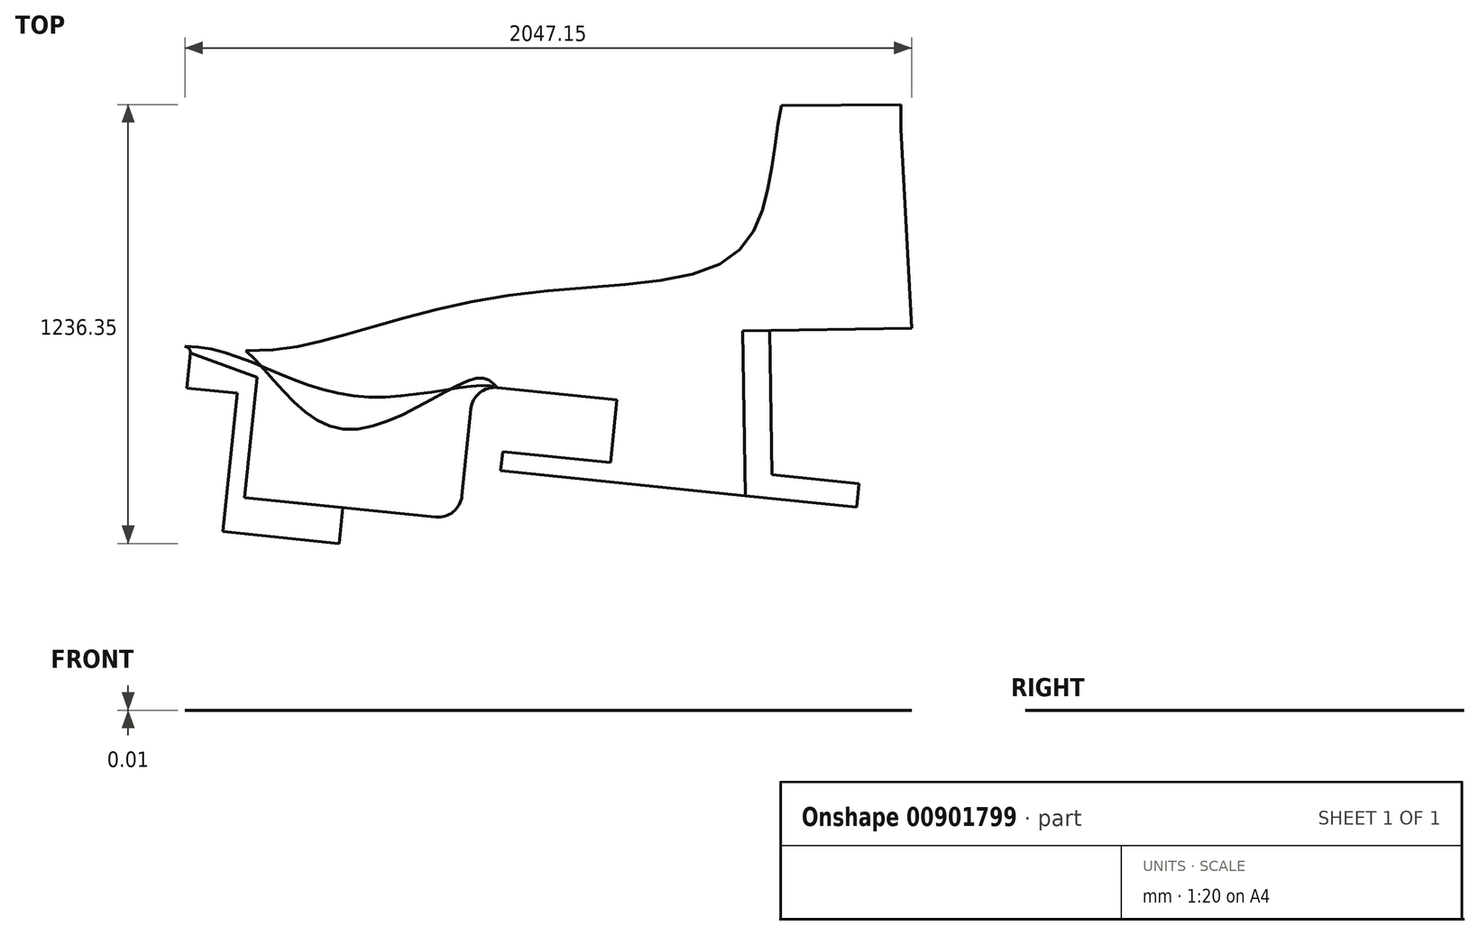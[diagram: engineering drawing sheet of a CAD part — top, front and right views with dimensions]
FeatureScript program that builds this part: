
annotation { "Feature Type Name" : "Feature", "Feature Type Description" : "" }
export const myFeature = defineFeature(function(context is Context, id is Id, definition is map)
    precondition{}
    {
        {
            var Q0;
            Q0=qCreatedBy(makeId("Top.planeOp"),FACE);
            var sketch = newSketch(context, id + "F0", { "sketchPlane" : qUnion([Q0])});
            skLineSegment(sketch, "E0", {"start": v(0, 0) * mm, "end": v(280.83, -5741.92) * mm});
            skLineSegment(sketch, "E1", {"start": v(0, 0) * mm, "end": v(-5127.58, -2299.89) * mm});
            skLineSegment(sketch, "E2", {"start": v(-5127.58, -2299.89) * mm, "end": v(-4076.75, -4642.7) * mm});
            skLineSegment(sketch, "E3", {"start": v(280.83, -5741.92) * mm, "end": v(-3052.99, -5385.64) * mm});
            skArc(sketch, "E4", {"start": v(-3052.99, -5385.64) * mm, "mid": v(-3663.95, -5150.7) * mm, "end": v(-4076.75, -4642.7) * mm});
            skLineSegment(sketch, "E5", {"start": v(-1078.04, -3852) * mm, "end": v(-1142.99, -4483.67) * mm});
            skLineSegment(sketch, "E6", {"start": v(-1142.99, -4483.67) * mm, "end": v(-2406.33, -4353.77) * mm});
            skLineSegment(sketch, "E7", {"start": v(-2406.33, -4353.77) * mm, "end": v(-2341.38, -3722.1) * mm});
            skLineSegment(sketch, "E8", {"start": v(-2341.38, -3722.1) * mm, "end": v(-1078.04, -3852) * mm});
            skLineSegment(sketch, "E9", {"start": v(-4856.16, 2242.88) * mm, "end": v(-4856.16, 467.27) * mm});
            skSolve(sketch);
        }
        {
            var Q0;
            Q0=qCreatedBy(makeId("Top.planeOp"),FACE);
            var sketch = newSketch(context, id + "F1", { "sketchPlane" : qUnion([Q0])});
            skLineSegment(sketch, "E10.0", {"start": v(0, 0) * mm, "end": v(-5127.58, -2299.89) * mm});
            skLineSegment(sketch, "E11.0", {"start": v(0, 0) * mm, "end": v(280.83, -5741.92) * mm});
            skLineSegment(sketch, "E12.0", {"start": v(280.83, -5741.92) * mm, "end": v(-3052.99, -5385.64) * mm, "construction": true});
            skLineSegment(sketch, "E13.0", {"start": v(-5127.58, -2299.89) * mm, "end": v(-4076.75, -4642.7) * mm, "construction": true});
            skArc(sketch, "E14.0", {"start": v(-3052.99, -5385.64) * mm, "mid": v(-3663.95, -5150.7) * mm, "end": v(-4076.75, -4642.7) * mm, "construction": true});
            skLineSegment(sketch, "E15", {"start": v(-4611.92, -4434.06) * mm, "end": v(-4436.1, -4508.99) * mm});
            skLineSegment(sketch, "E16", {"start": v(-4492.1, -4650.67) * mm, "end": v(-4694.79, -4576.67) * mm});
            skLineSegment(sketch, "E17", {"start": v(-4694.79, -4576.67) * mm, "end": v(-4659.04, -5600.24) * mm});
            skPoint(sketch, "E18.visualSharp", {"position": v(-4703.1, -4395.2) * mm});
            skArc(sketch, "E18.filletArc", {"start": v(-4704.54, -4297.44) * mm, "mid": v(-4678.33, -4379.37) * mm, "end": v(-4611.92, -4434.06) * mm});
            skArc(sketch, "E19.filletArc", {"start": v(-4492.1, -4650.67) * mm, "mid": v(-4395.1, -4607.1) * mm, "end": v(-4436.1, -4508.99) * mm});
            skCircle(sketch, "E20", {"center": v(-4268.28, -4085.71) * mm, "radius": 5.3 * mm});
            skArc(sketch, "E21.filletArc", {"start": v(-4659.04, -5600.24) * mm, "mid": v(-4591.11, -5764.44) * mm, "end": v(-4432.19, -5843.93) * mm});
            skLineSegment(sketch, "E22", {"start": v(280.83, -5741.92) * mm, "end": v(310.6, -6350.8) * mm});
            skLineSegment(sketch, "E23", {"start": v(310.6, -6350.8) * mm, "end": v(-3023.21, -5994.5) * mm});
            skLineSegment(sketch, "E24", {"start": v(-3023.21, -5994.5) * mm, "end": v(-4432.19, -5843.93) * mm});
            skPoint(sketch, "E25", {"position": v(-4651.35, -5820.51) * mm});
            skArc(sketch, "E26", {"start": v(-4898.36, -3559.15) * mm, "mid": v(-4790.33, -3925.37) * mm, "end": v(-4704.54, -4297.44) * mm});
            skLineSegment(sketch, "E27", {"start": v(-4898.36, -3559.15) * mm, "end": v(-5287.82, -2371.76) * mm});
            skLineSegment(sketch, "E28", {"start": v(-5127.58, -2299.89) * mm, "end": v(-5287.82, -2371.76) * mm});
            skSolve(sketch);
        }
        {
            var Q0;
            Q0=qCreatedBy(makeId("Top.planeOp"),FACE);
            var sketch = newSketch(context, id + "F2", { "sketchPlane" : qUnion([Q0])});
            skLineSegment(sketch, "E29.0", {"start": v(-1142.99, -4483.67) * mm, "end": v(-2406.33, -4353.77) * mm});
            skLineSegment(sketch, "E29.1", {"start": v(-2406.33, -4353.77) * mm, "end": v(-2341.38, -3722.1) * mm});
            skLineSegment(sketch, "E29.2", {"start": v(-2341.38, -3722.1) * mm, "end": v(-1078.04, -3852) * mm});
            skLineSegment(sketch, "E29.3", {"start": v(-1078.04, -3852) * mm, "end": v(-1142.99, -4483.67) * mm});
            skSolve(sketch);
        }
        {
            var Q0;
            Q0=qCreatedBy(makeId("Top.planeOp"),FACE);
            var sketch = newSketch(context, id + "F3", { "sketchPlane" : qUnion([Q0])});
            skLineSegment(sketch, "E30.bottom", {"start": v(-1746.23, -4421.65) * mm, "end": v(-2406.33, -4353.77) * mm});
            skLineSegment(sketch, "E30.top", {"start": v(-1756.63, -4522.71) * mm, "end": v(-2416.72, -4454.84) * mm});
            skLineSegment(sketch, "E30.left", {"start": v(-1746.23, -4421.65) * mm, "end": v(-1756.63, -4522.71) * mm});
            skLineSegment(sketch, "E30.right", {"start": v(-2406.33, -4353.77) * mm, "end": v(-2416.72, -4454.84) * mm});
            skSolve(sketch);
        }
        {
            var Q0;
            Q0=qCreatedBy(makeId("Top.planeOp"),FACE);
            var sketch = newSketch(context, id + "F4", { "sketchPlane" : qUnion([Q0])});
            skLineSegment(sketch, "E31.0", {"start": v(-76.06, -3709.36) * mm, "end": v(-1078.4, -3607.27) * mm});
            skLineSegment(sketch, "E31.1", {"start": v(-159.73, -4492.3) * mm, "end": v(-76.06, -3709.36) * mm});
            skLineSegment(sketch, "E31.2", {"start": v(-333.92, -4915.03) * mm, "end": v(-159.73, -4492.3) * mm});
            skLineSegment(sketch, "E31.3", {"start": v(-470.25, -6190.7) * mm, "end": v(-333.92, -4915.03) * mm});
            skLineSegment(sketch, "E31.4", {"start": v(-677.27, -4920.95) * mm, "end": v(-809.1, -6154.5) * mm});
            skLineSegment(sketch, "E32", {"start": v(-1078.4, -3607.27) * mm, "end": v(-1103.3, -3849.4) * mm});
            skArc(sketch, "E33", {"start": v(-677.27, -4920.95) * mm, "mid": v(-675.84, -4893.96) * mm, "end": v(-677.27, -4866.97) * mm});
            skLineSegment(sketch, "E34", {"start": v(-913.54, -4528.55) * mm, "end": v(-947.23, -4504.19) * mm, "construction": true});
            skArc(sketch, "E35", {"start": v(-677.27, -4866.97) * mm, "mid": v(-710.72, -4746.63) * mm, "end": v(-781.3, -4643.58) * mm});
            skArc(sketch, "E36", {"start": v(-781.3, -4643.58) * mm, "mid": v(-844.83, -4583.09) * mm, "end": v(-913.54, -4528.55) * mm});
            skLineSegment(sketch, "E37", {"start": v(-913.54, -4528.55) * mm, "end": v(-1143.42, -4487.89) * mm});
            skLineSegment(sketch, "E38", {"start": v(-1097.45, -4496.02) * mm, "end": v(-1031.28, -3852.56) * mm});
            skLineSegment(sketch, "E39", {"start": v(-1031.28, -3852.56) * mm, "end": v(-1103.3, -3845.15) * mm});
            skArc(sketch, "E40.filletArc", {"start": v(-892.97, -6222.17) * mm, "mid": v(-837.02, -6205.7) * mm, "end": v(-809.1, -6154.5) * mm});
            skArc(sketch, "E41.filletArc", {"start": v(-470.25, -6190.7) * mm, "mid": v(-453.78, -6246.66) * mm, "end": v(-402.58, -6274.57) * mm});
            skLineSegment(sketch, "E42", {"start": v(-402.58, -6274.57) * mm, "end": v(-892.97, -6222.17) * mm});
            skSolve(sketch);
        }
        {
            var Q0;
            Q0=qCreatedBy(makeId("Top.planeOp"),FACE);
            var sketch = newSketch(context, id + "F5", { "sketchPlane" : qUnion([Q0])});
            skPoint(sketch, "E43.0", {"position": v(-67.96, -3633.6) * mm});
            skCircle(sketch, "E44", {"center": v(-67.96, -3633.6) * mm, "radius": 2.51 * mm});
            skCircle(sketch, "E45.1.0.0", {"center": v(-270.12, -3613) * mm, "radius": 2.51 * mm});
            skCircle(sketch, "E45.2.0.0", {"center": v(-472.27, -3592.41) * mm, "radius": 2.51 * mm});
            skLineSegment(sketch, "E45.direction1", {"start": v(-67.96, -3633.6) * mm, "end": v(-270.12, -3613) * mm, "construction": true});
            skLineSegment(sketch, "E45.direction2", {"start": v(-67.96, -3633.6) * mm, "end": v(104.71, -3651.18) * mm, "construction": true});
            skCircle(sketch, "E46.0.3.0", {"center": v(-674.42, -3571.82) * mm, "radius": 2.51 * mm});
            skCircle(sketch, "E47.0.4.0", {"center": v(-876.58, -3551.23) * mm, "radius": 2.51 * mm});
            skCircle(sketch, "E48.0.5.0", {"center": v(-1078.73, -3530.64) * mm, "radius": 2.51 * mm});
            skCircle(sketch, "E49", {"center": v(104.71, -3651.18) * mm, "radius": 2.51 * mm});
            skLineSegment(sketch, "E50.bottom", {"start": v(-1107.9, -3817.5) * mm, "end": v(-1100.52, -3818.26) * mm});
            skLineSegment(sketch, "E50.top", {"start": v(-1108.65, -3824.88) * mm, "end": v(-1101.28, -3825.63) * mm});
            skLineSegment(sketch, "E50.left", {"start": v(-1107.9, -3817.5) * mm, "end": v(-1108.65, -3824.88) * mm});
            skLineSegment(sketch, "E50.right", {"start": v(-1100.52, -3818.26) * mm, "end": v(-1101.28, -3825.63) * mm});
            skPoint(sketch, "E50.middle", {"position": v(-1104.59, -3821.57) * mm});
            skLineSegment(sketch, "E51.bottom", {"start": v(-1098.38, -3729.12) * mm, "end": v(-1091.01, -3729.87) * mm});
            skLineSegment(sketch, "E51.top", {"start": v(-1099.14, -3736.49) * mm, "end": v(-1091.77, -3737.24) * mm});
            skLineSegment(sketch, "E51.left", {"start": v(-1098.38, -3729.12) * mm, "end": v(-1099.14, -3736.49) * mm});
            skLineSegment(sketch, "E51.right", {"start": v(-1091.01, -3729.87) * mm, "end": v(-1091.77, -3737.24) * mm});
            skPoint(sketch, "E51.middle", {"position": v(-1095.08, -3733.18) * mm});
            skSolve(sketch);
        }
        {
            var Q0;
            Q0=makeQuery(id+"F0.imprint","IMPRINT",FACE,{"disambiguationData":[TD([[makeQuery(id+"F0.imprint","IMPRINT",EDGE,{"derivedFrom":sQuery(id+"F0.wireOp",EDGE,"E0")}),-1.0]])]});
            var sketch = newSketch(context, id + "F6", { "sketchPlane" : qUnion([Q0])});
            skLineSegment(sketch, "E52.0", {"start": v(-1142.99, -4483.67) * mm, "end": v(-2406.33, -4353.77) * mm});
            skLineSegment(sketch, "E53", {"start": v(-1142.99, -4483.67) * mm, "end": v(-1160.74, -4656.33) * mm});
            skLineSegment(sketch, "E54", {"start": v(-1160.74, -4656.33) * mm, "end": v(-1194.43, -4652.87) * mm});
            skLineSegment(sketch, "E55", {"start": v(-1194.43, -4652.87) * mm, "end": v(-1176.68, -4480.2) * mm});
            skLineSegment(sketch, "E56", {"start": v(-1122.99, -4736.81) * mm, "end": v(-1926.54, -4654.19) * mm});
            skLineSegment(sketch, "E57", {"start": v(-1926.54, -4654.19) * mm, "end": v(-1911.06, -4503.64) * mm});
            skLineSegment(sketch, "E58", {"start": v(-1767.15, -4593.98) * mm, "end": v(-1160.74, -4656.33) * mm});
            skLineSegment(sketch, "E59", {"start": v(-1125.7, -4742.92) * mm, "end": v(-971.39, -4574.26) * mm});
            skLineSegment(sketch, "E60", {"start": v(-971.39, -4574.26) * mm, "end": v(-796.53, -4817.92) * mm});
            skLineSegment(sketch, "E61", {"start": v(-778.05, -4887.95) * mm, "end": v(-871.1, -5758.64) * mm});
            skLineSegment(sketch, "E62", {"start": v(-871.1, -5758.64) * mm, "end": v(-908.99, -5754.59) * mm});
            skLineSegment(sketch, "E63", {"start": v(-908.99, -5754.59) * mm, "end": v(-816.85, -4892.39) * mm});
            skLineSegment(sketch, "E64", {"start": v(-832.46, -4833.2) * mm, "end": v(-974.97, -4634.62) * mm});
            skLineSegment(sketch, "E65", {"start": v(-974.97, -4634.62) * mm, "end": v(-1097.6, -4768.64) * mm});
            skLineSegment(sketch, "E66", {"start": v(-1097.6, -4768.64) * mm, "end": v(-1125.7, -4742.92) * mm});
            skLineSegment(sketch, "E67", {"start": v(-1160.74, -4656.33) * mm, "end": v(-1122.99, -4736.81) * mm});
            skLineSegment(sketch, "E68", {"start": v(-936.32, -4535.93) * mm, "end": v(-971.39, -4574.26) * mm});
            skLineSegment(sketch, "E69", {"start": v(-1142.99, -4483.67) * mm, "end": v(-1007.92, -4509.88) * mm});
            skLineSegment(sketch, "E70", {"start": v(-1007.92, -4509.88) * mm, "end": v(-936.32, -4535.93) * mm});
            skLineSegment(sketch, "E71", {"start": v(-1007.92, -4509.88) * mm, "end": v(-1160.74, -4656.33) * mm});
            skLineSegment(sketch, "E72", {"start": v(-1134.76, -4631.43) * mm, "end": v(-1080.63, -4693.66) * mm, "construction": true});
            skLineSegment(sketch, "E73", {"start": v(-1106.5, -4604.34) * mm, "end": v(-1041.34, -4650.71) * mm, "construction": true});
            skPoint(sketch, "E74.visualSharp", {"position": v(-813.36, -4859.82) * mm});
            skArc(sketch, "E74.filletArc", {"start": v(-816.85, -4892.39) * mm, "mid": v(-819.2, -4861.36) * mm, "end": v(-832.46, -4833.2) * mm});
            skPoint(sketch, "E75.visualSharp", {"position": v(-773.94, -4849.41) * mm});
            skArc(sketch, "E75.filletArc", {"start": v(-778.05, -4887.95) * mm, "mid": v(-780.84, -4851.24) * mm, "end": v(-796.53, -4817.92) * mm});
            skLineSegment(sketch, "E76.bottom", {"start": v(-936.32, -4535.93) * mm, "end": v(-921.24, -4543.63) * mm, "construction": true});
            skLineSegment(sketch, "E76.top", {"start": v(-928.62, -4520.85) * mm, "end": v(-913.54, -4528.55) * mm, "construction": true});
            skLineSegment(sketch, "E76.left", {"start": v(-936.32, -4535.93) * mm, "end": v(-928.62, -4520.85) * mm, "construction": true});
            skLineSegment(sketch, "E76.right", {"start": v(-921.24, -4543.63) * mm, "end": v(-913.54, -4528.55) * mm, "construction": true});
            skPoint(sketch, "E76.middle", {"position": v(-924.93, -4532.24) * mm});
            skLineSegment(sketch, "E77", {"start": v(-913.54, -4528.55) * mm, "end": v(-936.32, -4535.93) * mm, "construction": true});
            skLineSegment(sketch, "E78", {"start": v(-1759.46, -4519.23) * mm, "end": v(-1767.15, -4593.98) * mm});
            skLineSegment(sketch, "E79", {"start": v(-1759.46, -4519.23) * mm, "end": v(-1911.06, -4503.64) * mm});
            skSolve(sketch);
        }
        {
            var Q0;
            Q0=qCreatedBy(makeId("Top.planeOp"),FACE);
            var sketch = newSketch(context, id + "F7", { "sketchPlane" : qUnion([Q0])});
            skLineSegment(sketch, "E80.bottom", {"start": v(-1532.84, -3805.24) * mm, "end": v(-1103.3, -3849.4) * mm});
            skLineSegment(sketch, "E80.top", {"start": v(-1522.45, -3704.17) * mm, "end": v(-1261.36, -3731.02) * mm});
            skLineSegment(sketch, "E80.left", {"start": v(-1532.84, -3805.24) * mm, "end": v(-1522.45, -3704.17) * mm});
            skLineSegment(sketch, "E80.right", {"start": v(-1103.3, -3849.4) * mm, "end": v(-1092.91, -3748.34) * mm});
            skLineSegment(sketch, "E81.top", {"start": v(-1053.94, -3369.34) * mm, "end": v(-1087.63, -3365.87) * mm});
            skLineSegment(sketch, "E81.left", {"start": v(-1092.91, -3748.34) * mm, "end": v(-1072.13, -3546.2) * mm});
            skLineSegment(sketch, "E81.right", {"start": v(-1187.05, -3670.57) * mm, "end": v(-1161.94, -3426.32) * mm});
            skLineSegment(sketch, "E82.bottom", {"start": v(-1053.94, -3369.34) * mm, "end": v(-750.74, -3400.51) * mm});
            skLineSegment(sketch, "E82.top", {"start": v(-1072.13, -3546.2) * mm, "end": v(-768.93, -3577.38) * mm});
            skLineSegment(sketch, "E82.right", {"start": v(-750.74, -3400.51) * mm, "end": v(-768.93, -3577.38) * mm});
            skPoint(sketch, "E83.visualSharp", {"position": v(-1193.98, -3737.95) * mm});
            skArc(sketch, "E83.filletArc", {"start": v(-1261.36, -3731.02) * mm, "mid": v(-1211.68, -3716.18) * mm, "end": v(-1187.05, -3670.57) * mm});
            skPoint(sketch, "E84.visualSharp", {"position": v(-1155, -3358.95) * mm});
            skArc(sketch, "E84.filletArc", {"start": v(-1087.63, -3365.87) * mm, "mid": v(-1137.3, -3380.7) * mm, "end": v(-1161.94, -3426.32) * mm});
            skLineSegment(sketch, "E85.bottom", {"start": v(-913, -3281.7) * mm, "end": v(-849.84, -3288.19) * mm});
            skLineSegment(sketch, "E85.top", {"start": v(-920.8, -3357.5) * mm, "end": v(-857.64, -3363.99) * mm});
            skLineSegment(sketch, "E85.left", {"start": v(-913, -3281.7) * mm, "end": v(-920.8, -3357.5) * mm});
            skLineSegment(sketch, "E85.right", {"start": v(-849.84, -3288.19) * mm, "end": v(-857.64, -3363.99) * mm});
            skSolve(sketch);
        }
        {
            var Q0;
            Q0=qCreatedBy(makeId("Top.planeOp"),FACE);
            var sketch = newSketch(context, id + "F8", { "sketchPlane" : qUnion([Q0])});
            skLineSegment(sketch, "E86.0", {"start": v(-2341.38, -3722.1) * mm, "end": v(-1078.04, -3852) * mm, "construction": true});
            skLineSegment(sketch, "E87", {"start": v(-2321.37, -3724.16) * mm, "end": v(-2281.32, -3334.63) * mm});
            skLineSegment(sketch, "E88", {"start": v(-2281.32, -3334.63) * mm, "end": v(-1820.2, -3382.04) * mm});
            skLineSegment(sketch, "E89", {"start": v(-1820.2, -3382.04) * mm, "end": v(-1860.25, -3771.57) * mm});
            skLineSegment(sketch, "E90", {"start": v(-1962.33, -3367.43) * mm, "end": v(-1952.15, -3268.47) * mm});
            skLineSegment(sketch, "E91", {"start": v(-1967.26, -3249.9) * mm, "end": v(-2110.44, -3235.17) * mm});
            skLineSegment(sketch, "E92", {"start": v(-2129.02, -3250.28) * mm, "end": v(-2139.2, -3349.24) * mm});
            skPoint(sketch, "E93", {"position": v(-2050.76, -3358.34) * mm});
            skPoint(sketch, "E94.visualSharp", {"position": v(-2127.29, -3233.44) * mm});
            skArc(sketch, "E94.filletArc", {"start": v(-2110.44, -3235.17) * mm, "mid": v(-2122.86, -3238.88) * mm, "end": v(-2129.02, -3250.28) * mm});
            skPoint(sketch, "E95.visualSharp", {"position": v(-1950.42, -3251.62) * mm});
            skArc(sketch, "E95.filletArc", {"start": v(-1952.15, -3268.47) * mm, "mid": v(-1955.86, -3256.05) * mm, "end": v(-1967.26, -3249.9) * mm});
            skLineSegment(sketch, "E96", {"start": v(-2321.37, -3724.16) * mm, "end": v(-1860.25, -3771.57) * mm});
            skPoint(sketch, "E97", {"position": v(-2038.85, -3242.53) * mm});
            skSolve(sketch);
        }
        {
            var Q0;
            Q0=qCreatedBy(makeId("Top.planeOp"),FACE);
            var sketch = newSketch(context, id + "F9", { "sketchPlane" : qUnion([Q0])});
            skLineSegment(sketch, "E98.bottom", {"start": v(-1868, -1510.12) * mm, "end": v(-293.22, -1501.78) * mm});
            skLineSegment(sketch, "E98.top", {"start": v(-1862.33, -2579.02) * mm, "end": v(-287.56, -2570.68) * mm});
            skLineSegment(sketch, "E98.left", {"start": v(-1868, -1510.12) * mm, "end": v(-1862.33, -2579.02) * mm});
            skLineSegment(sketch, "E98.right", {"start": v(-293.22, -1501.78) * mm, "end": v(-287.56, -2570.68) * mm});
            skLineSegment(sketch, "E99.bottom", {"start": v(-1447.2, -1829.63) * mm, "end": v(-532.81, -1824.78) * mm});
            skLineSegment(sketch, "E99.top", {"start": v(-1444.78, -2286.82) * mm, "end": v(-530.39, -2281.98) * mm});
            skLineSegment(sketch, "E99.left", {"start": v(-1447.2, -1829.63) * mm, "end": v(-1444.78, -2286.82) * mm});
            skLineSegment(sketch, "E99.right", {"start": v(-532.81, -1824.78) * mm, "end": v(-530.39, -2281.98) * mm});
            skLineSegment(sketch, "E100", {"start": v(48.99, -2568.9) * mm, "end": v(47.56, -1499.97) * mm, "construction": true});
            skPoint(sketch, "E101", {"position": v(-1062.36, -3368.47) * mm});
            skPoint(sketch, "E102", {"position": v(-1007.6, -2574.5) * mm});
            skLineSegment(sketch, "E103", {"start": v(-987.58, -2284.4) * mm, "end": v(-1040.59, -3052.82) * mm, "construction": true});
            skPoint(sketch, "E104", {"position": v(-1720.52, -2578.27) * mm});
            skPoint(sketch, "E105", {"position": v(-1858.1, -3378.15) * mm});
            skLineSegment(sketch, "E106", {"start": v(-1769.2, -2578.53) * mm, "end": v(-1671.84, -2578.01) * mm, "construction": true});
            skLineSegment(sketch, "E107", {"start": v(-1720.52, -2578.27) * mm, "end": v(-2038.85, -3242.53) * mm, "construction": true});
            skArc(sketch, "E108.0.startCap", {"start": v(-1772.06, -2553.57) * mm, "mid": v(-1695.82, -2526.73) * mm, "end": v(-1668.98, -2602.97) * mm});
            skArc(sketch, "E108.0.endCap", {"start": v(-1987.32, -3267.23) * mm, "mid": v(-2063.55, -3294.07) * mm, "end": v(-2090.4, -3217.83) * mm});
            skLineSegment(sketch, "E108.0.left", {"start": v(-1668.98, -2602.97) * mm, "end": v(-1987.32, -3267.23) * mm});
            skLineSegment(sketch, "E108.0.right", {"start": v(-1772.06, -2553.57) * mm, "end": v(-2090.4, -3217.83) * mm});
            skSolve(sketch);
        }
        {
            var Q0;
            Q0=qCreatedBy(makeId("Top.planeOp"),FACE);
            var sketch = newSketch(context, id + "F10", { "sketchPlane" : qUnion([Q0])});
            skLineSegment(sketch, "E109.0", {"start": v(49.08, -2636.7) * mm, "end": v(104.71, -3651.18) * mm});
            skLineSegment(sketch, "E109.1", {"start": v(47.72, -1620.7) * mm, "end": v(49.08, -2636.7) * mm});
            skLineSegment(sketch, "E109.2", {"start": v(-21.76, -200) * mm, "end": v(47.72, -1620.7) * mm});
            skPoint(sketch, "E110.0", {"position": v(165.69, -6335.3) * mm});
            skSolve(sketch);
        }
        {
            var Q0;
            Q0=qCreatedBy(makeId("Top.planeOp"),FACE);
            var sketch = newSketch(context, id + "F11", { "sketchPlane" : qUnion([Q0])});
            skLineSegment(sketch, "E111.0.0", {"start": v(30.74, -3559.94) * mm, "end": v(25.06, -3212.85) * mm});
            skLineSegment(sketch, "E111.0.1", {"start": v(25.06, -3212.85) * mm, "end": v(-314.62, -3218.4) * mm});
            skLineSegment(sketch, "E111.0.2", {"start": v(-314.62, -3218.4) * mm, "end": v(-308.94, -3565.5) * mm});
            skLineSegment(sketch, "E111.0.3", {"start": v(-308.94, -3565.5) * mm, "end": v(30.74, -3559.94) * mm});
            skLineSegment(sketch, "E112", {"start": v(-313.48, -3611.51) * mm, "end": v(108.52, -3654.5) * mm});
            skLineSegment(sketch, "E113", {"start": v(108.52, -3654.5) * mm, "end": v(86.22, -3198.52) * mm});
            skLineSegment(sketch, "E114", {"start": v(86.22, -3198.52) * mm, "end": v(-320.13, -3205.17) * mm});
            skLineSegment(sketch, "E115", {"start": v(-320.13, -3205.17) * mm, "end": v(-313.48, -3611.51) * mm});
            skPoint(sketch, "E116", {"position": v(-308.18, -3612.05) * mm});
            skPoint(sketch, "E117", {"position": v(32.16, -3646.72) * mm});
            skSolve(sketch);
        }
        {
            var Q0;
            Q0=qCreatedBy(makeId("Top.planeOp"),FACE);
            var sketch = newSketch(context, id + "F12", { "sketchPlane" : qUnion([Q0])});
            skLineSegment(sketch, "E118", {"start": v(-68.63, -3636.45) * mm, "end": v(-75.42, -3703.05) * mm});
            skLineSegment(sketch, "E119", {"start": v(-75.42, -3703.05) * mm, "end": v(-388.72, -3671.13) * mm});
            skLineSegment(sketch, "E120", {"start": v(-388.72, -3671.13) * mm, "end": v(-396.32, -3206.41) * mm});
            skLineSegment(sketch, "E121", {"start": v(-396.32, -3206.41) * mm, "end": v(-320.13, -3205.17) * mm});
            skLineSegment(sketch, "E122.0", {"start": v(-320.13, -3205.17) * mm, "end": v(-313.48, -3611.51) * mm});
            skLineSegment(sketch, "E122.1", {"start": v(-313.48, -3611.51) * mm, "end": v(108.52, -3654.5) * mm});
            skSolve(sketch);
        }
        {
            var Q0;
            Q0=qCreatedBy(makeId("Top.planeOp"),FACE);
            var sketch = newSketch(context, id + "F13", { "sketchPlane" : qUnion([Q0])});
            skLineSegment(sketch, "E123.0", {"start": v(-1962.33, -3367.43) * mm, "end": v(-1952.15, -3268.47) * mm});
            skLineSegment(sketch, "E123.1", {"start": v(-2281.32, -3334.63) * mm, "end": v(-1820.2, -3382.04) * mm});
            skLineSegment(sketch, "E123.2", {"start": v(-1820.2, -3382.04) * mm, "end": v(-1860.25, -3771.57) * mm});
            skLineSegment(sketch, "E123.3", {"start": v(-2341.38, -3722.1) * mm, "end": v(-1078.04, -3852) * mm});
            skLineSegment(sketch, "E123.4", {"start": v(-1532.84, -3805.24) * mm, "end": v(-1522.45, -3704.17) * mm});
            skLineSegment(sketch, "E124", {"start": v(-1522.45, -3704.17) * mm, "end": v(-1799.33, -3675.7) * mm});
            skLineSegment(sketch, "E125", {"start": v(-1799.33, -3675.7) * mm, "end": v(-1764.47, -3336.7) * mm});
            skLineSegment(sketch, "E126", {"start": v(-1764.47, -3336.7) * mm, "end": v(-1952.15, -3268.47) * mm});
            skSolve(sketch);
        }
        {
            var Q0;
            Q0=qCreatedBy(makeId("Top.planeOp"),FACE);
            var sketch = newSketch(context, id + "F14", { "sketchPlane" : qUnion([Q0])});
            skFitSpline(sketch, "E127", {"points": [v(-1967.26, -3249.9) * mm, v(-1486.2, -3390.26) * mm, v(-1087.63, -3365.87) * mm], "startDerivative": vector(844.43, 20.7) * mm, "endDerivative": vector(377.93, -162.87) * mm});
            skArc(sketch, "E128.0", {"start": v(-1087.63, -3365.87) * mm, "mid": v(-1137.3, -3380.7) * mm, "end": v(-1161.94, -3426.32) * mm});
            skLineSegment(sketch, "E128.1", {"start": v(-1187.05, -3670.57) * mm, "end": v(-1161.94, -3426.32) * mm});
            skArc(sketch, "E128.2", {"start": v(-1261.36, -3731.02) * mm, "mid": v(-1211.68, -3716.18) * mm, "end": v(-1187.05, -3670.57) * mm});
            skLineSegment(sketch, "E128.3", {"start": v(-1522.45, -3704.17) * mm, "end": v(-1261.36, -3731.02) * mm});
            skLineSegment(sketch, "E128.4", {"start": v(-1522.45, -3704.17) * mm, "end": v(-1799.33, -3675.7) * mm});
            skLineSegment(sketch, "E128.5", {"start": v(-1799.33, -3675.7) * mm, "end": v(-1764.47, -3336.7) * mm});
            skLineSegment(sketch, "E128.6", {"start": v(-1764.47, -3336.7) * mm, "end": v(-1952.15, -3268.47) * mm});
            skArc(sketch, "E128.7", {"start": v(-1952.15, -3268.47) * mm, "mid": v(-1955.86, -3256.05) * mm, "end": v(-1967.26, -3249.9) * mm});
            skSolve(sketch);
        }
        {
            var Q0;
            Q0=qCreatedBy(makeId("Top.planeOp"),FACE);
            var sketch = newSketch(context, id + "F15", { "sketchPlane" : qUnion([Q0])});
            skFitSpline(sketch, "E129", {"points": [v(-1967.26, -3249.9) * mm, v(-1560.5, -3229.59) * mm, v(-1033.9, -3102.67) * mm, v(-440.8, -3006.53) * mm, v(-320.87, -2783.9) * mm, v(-287.56, -2570.68) * mm], "startDerivative": vector(2971.03, -351.05) * mm, "endDerivative": vector(268.32, 1341.87) * mm});
            skLineSegment(sketch, "E130", {"start": v(-287.56, -2570.68) * mm, "end": v(48.99, -2568.9) * mm});
            skLineSegment(sketch, "E131.0", {"start": v(47.72, -1620.7) * mm, "end": v(49.08, -2636.7) * mm});
            skLineSegment(sketch, "E131.1", {"start": v(49.08, -2636.7) * mm, "end": v(104.71, -3651.18) * mm});
            skLineSegment(sketch, "E131.2", {"start": v(86.22, -3198.52) * mm, "end": v(-320.13, -3205.17) * mm});
            skLineSegment(sketch, "E131.3", {"start": v(-396.32, -3206.41) * mm, "end": v(-320.13, -3205.17) * mm});
            skLineSegment(sketch, "E131.4", {"start": v(-388.72, -3671.13) * mm, "end": v(-396.32, -3206.41) * mm});
            skLineSegment(sketch, "E131.6", {"start": v(-750.74, -3400.51) * mm, "end": v(-768.93, -3577.38) * mm});
            skLineSegment(sketch, "E131.7", {"start": v(-1072.13, -3546.2) * mm, "end": v(-768.93, -3577.38) * mm});
            skLineSegment(sketch, "E131.8", {"start": v(-1092.91, -3748.34) * mm, "end": v(-1072.13, -3546.2) * mm});
            skLineSegment(sketch, "E131.9", {"start": v(-1053.94, -3369.34) * mm, "end": v(-750.74, -3400.51) * mm});
            skLineSegment(sketch, "E131.10", {"start": v(-1053.94, -3369.34) * mm, "end": v(-1087.63, -3365.87) * mm});
            skFitSpline(sketch, "E131.11", {"points": [v(-1967.26, -3249.9) * mm, v(-1818.54, -3246.25) * mm, v(-1527.83, -3482.55) * mm, v(-1147.05, -3340.27) * mm, v(-1087.63, -3365.87) * mm]});
            skLineSegment(sketch, "E132", {"start": v(-388.72, -3671.13) * mm, "end": v(-1077.69, -3600.3) * mm});
            skSolve(sketch);
        }
        {
            var Q0;
            {var subQ4=sQuery(id+"F13.wireOp",EDGE,"E123.0");Q0=makeQuery(id+"F13.imprint","IMPRINT",FACE,{"disambiguationData":[TD([[makeQuery(id+"F13.imprint","IMPRINT",EDGE,{"derivedFrom":subQ4}),-1.0]])]});}
            var Q1;
            Q1=makeQuery(id+"F14.imprint","IMPRINT",FACE,{"disambiguationData":[TD([[makeQuery(id+"F14.imprint","IMPRINT",EDGE,{"derivedFrom":sQuery(id+"F14.wireOp",EDGE,"E127")}),-1.0]])]});
            var Q2;
            {var subQ7=sQuery(id+"F15.wireOp",EDGE,"E130");Q2=makeQuery(id+"F15.imprint","IMPRINT",FACE,{"disambiguationData":[TD([[makeQuery(id+"F15.imprint","IMPRINT",EDGE,{"derivedFrom":subQ7}),-1.0]])]});}
            var Q3;
            {var subQ0=sQuery(id+"F12.wireOp",EDGE,"E118");Q3=makeQuery(id+"F12.imprint","IMPRINT",FACE,{"disambiguationData":[TD([[makeQuery(id+"F12.imprint","IMPRINT",EDGE,{"derivedFrom":subQ0}),-1.0]])]});}
            extrude(context, id + "F16", {"entities" : qUnion([Q0, Q1, Q2, Q3]), "flatOperationType" : FlatOperationType.REMOVE, "depth" : 4 / 304.8 * mm, "offsetDistance" : 25.4 * mm, "domain" : OperationDomain.MODEL});
        }
    });
